# Revit family: Toilet_Seat-American_Standard-Advance_Clean-8012A80GRC.020
name_source: partatom
category: Specialty Equipment
revit_build: Autodesk Revit 2018 (Build: 20170223_1515(x64)
units: mm (PartAtom-declared; Revit-internal decimal feet)

## family parameters
Always vertical = No
Cut with Voids When Loaded = No
OmniClass Number = 23.45.05.21.14.11
OmniClass Title = Water Closet Seats
Part Type = Normal
Room Calculation Point = No
Round Connector Dimension = Use Diameter
Shared = Yes
Work Plane-Based = Yes

## types (1)
- 8012A80GRC.020
    Assembly Code = C1030200
    Default Elevation = 0"
    Description = American Standard Advanced Clean AC 2.0 SpaLet Seat With Remote Control Operation
    Height = 6 3/8"
    Hole Location = 5 1/2"
    IAPMO Compliance = ASME A112.4.2/CSA B45.16
    Installation Type = Surface Mounted
    Length = 16 3/4"
    Manufacturer = American Standard
    Material = Plastic-American Standard-020-White
    Model = 8012A80GRC.020
    Price = Prices may vary. Please consult Manufacturer Representative for most up-to-date price list.
    Product Documentation Link = https://www.americanstandard-us.com
    Product Page URL = https://www.americanstandard-us.com
    URL = https://www.americanstandard-us.com
    Warranty Information = 1 Year Limited Warranty
    Width = 21 1/2"

## geometry (parser evidence)
native form markers: Sweep x1
no freeform markers — native parametric forms only
